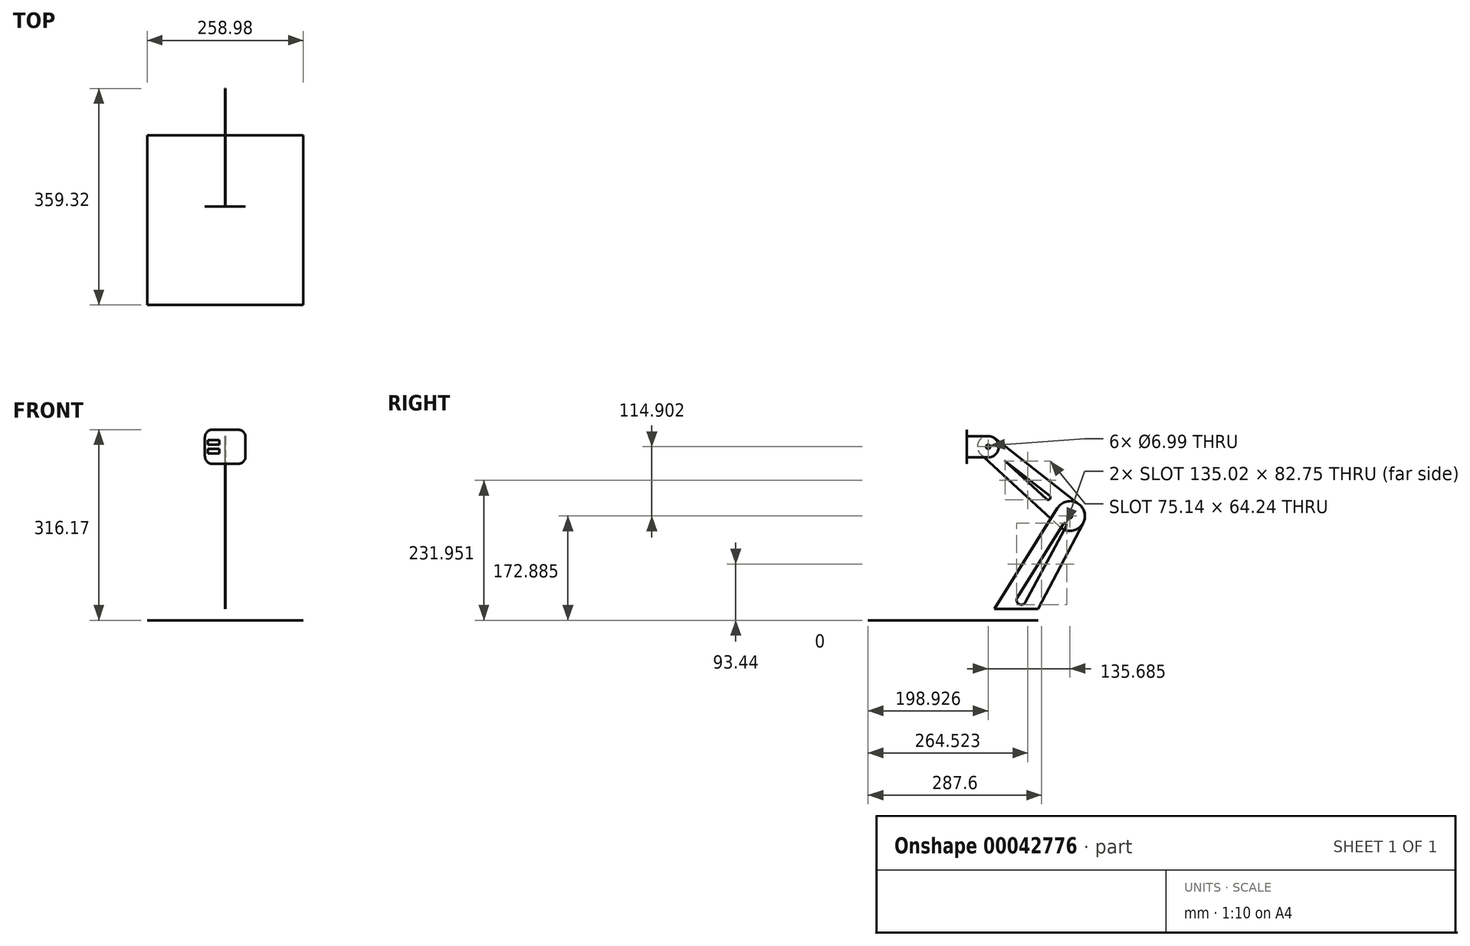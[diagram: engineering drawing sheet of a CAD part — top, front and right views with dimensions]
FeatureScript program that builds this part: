
annotation { "Feature Type Name" : "Feature", "Feature Type Description" : "" }
export const myFeature = defineFeature(function(context is Context, id is Id, definition is map)
    precondition{}
    {
        {
            assignVariable(context, id + "F0", {"name" : "thickness", "anyValue" : 3 / 101.6 * mm});
        }
        {
            var Q0;
            Q0=qCreatedBy(makeId("Top.planeOp"),FACE);
            var sketch = newSketch(context, id + "F1", { "sketchPlane" : qUnion([Q0])});
            skLineSegment(sketch, "E0.rect.bottom", {"start": v(129.5, -140.78) * mm, "end": v(-129.5, -140.78) * mm});
            skLineSegment(sketch, "E0.rect.top", {"start": v(129.5, 140.78) * mm, "end": v(-129.5, 140.78) * mm});
            skLineSegment(sketch, "E0.rect.left", {"start": v(129.5, -140.78) * mm, "end": v(129.5, 140.78) * mm});
            skLineSegment(sketch, "E0.rect.right", {"start": v(-129.5, -140.78) * mm, "end": v(-129.5, 140.78) * mm});
            skPoint(sketch, "E0.rect.middle", {"position": v(0, 0) * mm});
            skSolve(sketch);
        }
        {
            var Q0;
            Q0 = qSketchRegion(id + "F1", true);
            extrude(context, id + "F2", {"entities" : qUnion([Q0]), "depth" : getVariable(context, 'thickness')});
        }
        {
            var Q0;
            Q0=qCreatedBy(makeId("Right.planeOp"),FACE);
            cPlane(context, id + "F3", {"entities" : qUnion([Q0]), "cplaneType" : CPlaneType.OFFSET, "offset" : getVariable(context, 'thickness') / 2, "width" : 152.4 * mm, "height" : 152.4 * mm});
        }
        {
            var Q0;
            Q0=qCreatedBy(id+"F3.planeOp",FACE);
            var sketch = newSketch(context, id + "F4", { "sketchPlane" : qUnion([Q0])});
            skLineSegment(sketch, "E1", {"start": v(68.58, 19.05) * mm, "end": v(172.87, 185.98) * mm});
            skLineSegment(sketch, "E2", {"start": v(215.7, 161.37) * mm, "end": v(140.78, 19.05) * mm});
            skLineSegment(sketch, "E3", {"start": v(140.78, 19.05) * mm, "end": v(68.58, 19.05) * mm});
            skArc(sketch, "E4", {"start": v(172.87, 185.98) * mm, "mid": v(206.14, 194.31) * mm, "end": v(215.7, 161.37) * mm});
            skCircle(sketch, "E5", {"center": v(193.83, 172.88) * mm, "radius": 3.5 * mm});
            skLineSegment(sketch, "E6", {"start": v(182.6, 159.55) * mm, "end": v(106.54, 37.81) * mm});
            skLineSegment(sketch, "E7", {"start": v(187.85, 156.5) * mm, "end": v(120.04, 29.99) * mm});
            skLineSegment(sketch, "E8", {"start": v(193.83, 172.88) * mm, "end": v(104.68, 19.05) * mm, "construction": true});
            skArc(sketch, "E9", {"start": v(187.85, 156.5) * mm, "mid": v(186.7, 160.57) * mm, "end": v(182.6, 159.55) * mm});
            skArc(sketch, "E10", {"start": v(120.04, 29.99) * mm, "mid": v(109.24, 26.92) * mm, "end": v(106.54, 37.81) * mm});
            skSolve(sketch);
        }
        {
            var Q0;
            Q0 = qSketchRegion(id + "F4", true);
            extrude(context, id + "F5", {"entities" : qUnion([Q0]), "depth" : getVariable(context, 'thickness')});
        }
        {
            var Q0;
            Q0=makeQuery(id+"F5.opExtrude","SWEPT_BODY",BODY,{"disambiguationData":[OSD([sQuery(id+"F4.wireOp",EDGE,"E1"),sQuery(id+"F4.wireOp",EDGE,"54643f7f-2674-4445-8b05-3632952fac33"),sQuery(id+"F4.wireOp",EDGE,"E2"),sQuery(id+"F4.wireOp",EDGE,"E3")])]});
            var Q1;
            Q1=qCreatedBy(makeId("Right.planeOp"),FACE);
            mirror(context, id + "F6", {"entities" : qUnion([Q0]), "mirrorPlane" : qUnion([Q1])});
        }
        {
            var Q0;
            Q0=makeQuery(id+"F6.opPattern","COPY",FACE,{"derivedFrom":makeQuery(id+"F5.opExtrude","CAP_FACE",FACE,{"disambiguationData":[OSD([sQuery(id+"F4.wireOp",EDGE,"E1"),sQuery(id+"F4.wireOp",EDGE,"E2"),sQuery(id+"F4.wireOp",EDGE,"E3"),sQuery(id+"F4.wireOp",EDGE,"E4"),sQuery(id+"F4.wireOp",EDGE,"E5")])],"isStart":true}),"instanceName":"1"});
            var sketch = newSketch(context, id + "F7", { "sketchPlane" : qUnion([Q0])});
            skArc(sketch, "E11", {"start": v(177.13, 154.67) * mm, "mid": v(212.7, 156.91) * mm, "end": v(209.05, 192.36) * mm});
            skLineSegment(sketch, "E12", {"start": v(209.05, 192.36) * mm, "end": v(69.05, 301.74) * mm});
            skLineSegment(sketch, "E13", {"start": v(177.13, 154.67) * mm, "end": v(46.18, 274.73) * mm});
            skArc(sketch, "E14", {"start": v(46.18, 274.73) * mm, "mid": v(44.63, 299.23) * mm, "end": v(69.05, 301.74) * mm});
            skCircle(sketch, "E15", {"center": v(58.15, 287.79) * mm, "radius": 3.5 * mm});
            skCircle(sketch, "E16.0", {"center": v(193.83, 172.88) * mm, "radius": 3.5 * mm});
            skCircle(sketch, "E17", {"center": v(193.83, 172.88) * mm, "radius": 24.71 * mm, "construction": true});
            skCircle(sketch, "E18", {"center": v(58.15, 287.79) * mm, "radius": 17.71 * mm, "construction": true});
            skLineSegment(sketch, "E19", {"start": v(86.36, 264.05) * mm, "end": v(159.87, 206.6) * mm});
            skLineSegment(sketch, "E20", {"start": v(86.21, 263.87) * mm, "end": v(154.98, 200.82) * mm});
            skArc(sketch, "E21", {"start": v(86.21, 263.87) * mm, "mid": v(86.2, 264.03) * mm, "end": v(86.36, 264.05) * mm});
            skArc(sketch, "E22", {"start": v(154.98, 200.82) * mm, "mid": v(160.43, 201.17) * mm, "end": v(159.87, 206.6) * mm});
            skLineSegment(sketch, "E23", {"start": v(58.15, 287.79) * mm, "end": v(193.83, 172.88) * mm, "construction": true});
            skSolve(sketch);
        }
        {
            var Q0;
            Q0 = qSketchRegion(id + "F7", true);
            extrude(context, id + "F8", {"entities" : qUnion([Q0]), "depth" : getVariable(context, 'thickness')});
        }
        {
            var Q0;
            Q0=makeQuery(id+"F8.opExtrude","CAP_FACE",FACE,{"disambiguationData":[OSD([sQuery(id+"F7.wireOp",EDGE,"E11"),sQuery(id+"F7.wireOp",EDGE,"E12"),sQuery(id+"F7.wireOp",EDGE,"E13"),sQuery(id+"F7.wireOp",EDGE,"E14"),sQuery(id+"F7.wireOp",EDGE,"E15")])],"isStart":true});
            var sketch = newSketch(context, id + "F9", { "sketchPlane" : qUnion([Q0])});
            skArc(sketch, "E24", {"start": v(-58.15, 305.5) * mm, "mid": v(-75.86, 287.79) * mm, "end": v(-58.15, 270.07) * mm});
            skLineSegment(sketch, "E25", {"start": v(-58.15, 305.5) * mm, "end": v(-22.65, 305.5) * mm});
            skLineSegment(sketch, "E26", {"start": v(-22.65, 305.5) * mm, "end": v(-22.65, 270.07) * mm});
            skLineSegment(sketch, "E27", {"start": v(-22.65, 270.07) * mm, "end": v(-58.15, 270.07) * mm});
            skCircle(sketch, "E28.0", {"center": v(-58.15, 287.79) * mm, "radius": 3.5 * mm});
            skSolve(sketch);
        }
        {
            var Q0;
            Q0 = qSketchRegion(id + "F9", true);
            extrude(context, id + "F10", {"entities" : qUnion([Q0]), "depth" : getVariable(context, 'thickness')});
        }
        {
            var Q0;
            Q0=makeQuery(id+"F10.opExtrude","SWEPT_FACE",FACE,{"disambiguationData":[OSD([sQuery(id+"F9.wireOp",EDGE,"E26")])]});
            var sketch = newSketch(context, id + "F11", { "sketchPlane" : qUnion([Q0])});
            skLineSegment(sketch, "E29.bottom", {"start": v(-28.58, 298.93) * mm, "end": v(-9.53, 298.93) * mm});
            skLineSegment(sketch, "E29.top", {"start": v(-28.58, 291.07) * mm, "end": v(-9.53, 291.07) * mm});
            skLineSegment(sketch, "E29.left", {"start": v(-28.58, 298.93) * mm, "end": v(-28.58, 291.07) * mm});
            skLineSegment(sketch, "E29.right", {"start": v(-9.53, 298.93) * mm, "end": v(-9.53, 291.07) * mm});
            skLineSegment(sketch, "E30.bottom", {"start": v(-28.58, 284.5) * mm, "end": v(-9.53, 284.5) * mm});
            skLineSegment(sketch, "E30.top", {"start": v(-28.58, 276.64) * mm, "end": v(-9.53, 276.64) * mm});
            skLineSegment(sketch, "E30.left", {"start": v(-28.58, 284.5) * mm, "end": v(-28.58, 276.64) * mm});
            skLineSegment(sketch, "E30.right", {"start": v(-9.53, 284.5) * mm, "end": v(-9.53, 276.64) * mm});
            skLineSegment(sketch, "E31", {"start": v(-19.05, 305.5) * mm, "end": v(-19.05, 298.93) * mm, "construction": true});
            skLineSegment(sketch, "E32", {"start": v(-19.05, 291.07) * mm, "end": v(-19.05, 284.5) * mm, "construction": true});
            skLineSegment(sketch, "E33", {"start": v(-19.05, 276.64) * mm, "end": v(-19.05, 270.07) * mm, "construction": true});
            skSolve(sketch);
        }
        {
            var Q0;
            Q0 = qSketchRegion(id + "F11", true);
            extrude(context, id + "F12", {"entities" : qUnion([Q0]), "operationType" : NewBodyOperationType.ADD, "depth" : getVariable(context, 'thickness')});
        }
        {
            var Q0;
            Q0=makeQuery(id+"F10.opExtrude","SWEPT_BODY",BODY,{"disambiguationData":[OSD([sQuery(id+"F9.wireOp",EDGE,"E24"),sQuery(id+"F9.wireOp",EDGE,"E25"),sQuery(id+"F9.wireOp",EDGE,"E26"),sQuery(id+"F9.wireOp",EDGE,"E27")])]});
            var Q1;
            Q1=qCreatedBy(makeId("Right.planeOp"),FACE);
            mirror(context, id + "F13", {"entities" : qUnion([Q0]), "mirrorPlane" : qUnion([Q1])});
        }
        {
            var Q0;
            Q0=makeQuery(id+"F13.opPattern","COPY",FACE,{"derivedFrom":makeQuery(id+"F10.opExtrude","SWEPT_FACE",FACE,{"disambiguationData":[OSD([sQuery(id+"F9.wireOp",EDGE,"E26")])]}),"instanceName":"1"});
            var sketch = newSketch(context, id + "F14", { "sketchPlane" : qUnion([Q0])});
            skPoint(sketch, "E34.0", {"position": v(-28.58, 305.5) * mm});
            skPoint(sketch, "E34.1", {"position": v(28.58, 270.07) * mm});
            skPoint(sketch, "E34.2", {"position": v(-28.58, 270.07) * mm});
            skPoint(sketch, "E34.3", {"position": v(28.58, 305.5) * mm});
            skLineSegment(sketch, "E35", {"start": v(-28.57, 270.07) * mm, "end": v(28.58, 305.5) * mm, "construction": true});
            skLineSegment(sketch, "E36", {"start": v(-28.57, 305.5) * mm, "end": v(28.58, 270.07) * mm, "construction": true});
            skLineSegment(sketch, "E37.rect.bottom", {"start": v(33.67, 259.4) * mm, "end": v(-33.67, 259.4) * mm});
            skLineSegment(sketch, "E37.rect.top", {"start": v(33.67, 316.17) * mm, "end": v(-33.67, 316.17) * mm});
            skLineSegment(sketch, "E37.rect.left", {"start": v(33.67, 259.4) * mm, "end": v(33.67, 316.17) * mm});
            skLineSegment(sketch, "E37.rect.right", {"start": v(-33.67, 259.4) * mm, "end": v(-33.67, 316.17) * mm});
            skPoint(sketch, "E37.rect.middle", {"position": v(0, 287.79) * mm});
            skSolve(sketch);
        }
        {
            var Q0;
            Q0 = qSketchRegion(id + "F14", true);
            extrude(context, id + "F15", {"entities" : qUnion([Q0]), "depth" : getVariable(context, 'thickness')});
        }
        {
            var Q0;
            Q0=makeQuery(id+"F15.opExtrude","SWEPT_EDGE",EDGE,{"disambiguationData":[OSD([sQuery(id+"F14.wireOp",EDGE,"E37.rect.top"),sQuery(id+"F14.wireOp",EDGE,"E37.rect.right")])]});
            var Q1;
            Q1=makeQuery(id+"F15.opExtrude","SWEPT_EDGE",EDGE,{"disambiguationData":[OSD([sQuery(id+"F14.wireOp",EDGE,"E37.rect.top"),sQuery(id+"F14.wireOp",EDGE,"E37.rect.left")])]});
            var Q2;
            Q2=makeQuery(id+"F15.opExtrude","SWEPT_EDGE",EDGE,{"disambiguationData":[OSD([sQuery(id+"F14.wireOp",EDGE,"E37.rect.bottom"),sQuery(id+"F14.wireOp",EDGE,"E37.rect.left")])]});
            var Q3;
            Q3=makeQuery(id+"F15.opExtrude","SWEPT_EDGE",EDGE,{"disambiguationData":[OSD([sQuery(id+"F14.wireOp",EDGE,"E37.rect.bottom"),sQuery(id+"F14.wireOp",EDGE,"E37.rect.right")])]});
            fillet(context, id + "F16", {"entities" : qUnion([Q0, Q1, Q2, Q3]), "radius" : 12.7 * mm, "tangentPropagation" : true, "allowEdgeOverflow" : false});
        }
        {
            var Q0;
            Q0=makeQuery(id+"F10.opExtrude","SWEPT_BODY",BODY,{"disambiguationData":[OSD([sQuery(id+"F9.wireOp",EDGE,"E24"),sQuery(id+"F9.wireOp",EDGE,"E25"),sQuery(id+"F9.wireOp",EDGE,"E26"),sQuery(id+"F9.wireOp",EDGE,"E27"),sQuery(id+"F9.wireOp",EDGE,"E28.0")])]});
            var Q1;
            Q1=makeQuery(id+"F13.opPattern","COPY",BODY,{"derivedFrom":makeQuery(id+"F10.opExtrude","SWEPT_BODY",BODY,{"disambiguationData":[OSD([sQuery(id+"F9.wireOp",EDGE,"E24"),sQuery(id+"F9.wireOp",EDGE,"E25"),sQuery(id+"F9.wireOp",EDGE,"E26"),sQuery(id+"F9.wireOp",EDGE,"E27"),sQuery(id+"F9.wireOp",EDGE,"E28.0")])]}),"instanceName":"1"});
            var Q2;
            Q2=makeQuery(id+"F15.opExtrude","SWEPT_BODY",BODY,{"disambiguationData":[OSD([sQuery(id+"F14.wireOp",EDGE,"E37.rect.bottom"),sQuery(id+"F14.wireOp",EDGE,"E37.rect.top"),sQuery(id+"F14.wireOp",EDGE,"E37.rect.left"),sQuery(id+"F14.wireOp",EDGE,"E37.rect.right")])]});
            booleanBodies(context, id + "F17", {"operationType" : BooleanOperationType.SUBTRACTION, "tools" : qUnion([Q0, Q1]), "targets" : qUnion([Q2]), "keepTools" : true});
        }
    });
